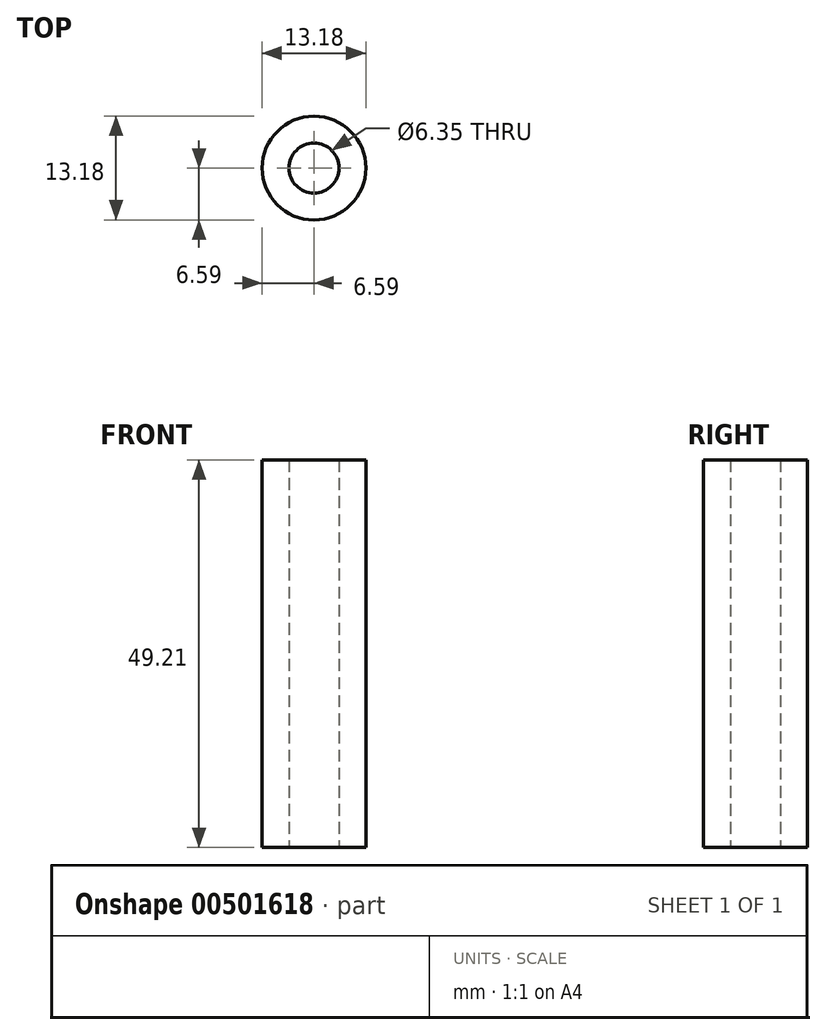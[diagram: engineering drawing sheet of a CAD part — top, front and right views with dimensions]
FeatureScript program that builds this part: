
annotation { "Feature Type Name" : "Feature", "Feature Type Description" : "" }
export const myFeature = defineFeature(function(context is Context, id is Id, definition is map)
    precondition{}
    {
        {
            var Q0;
            Q0=qCreatedBy(makeId("Top.planeOp"),FACE);
            var sketch = newSketch(context, id + "F0", { "sketchPlane" : qUnion([Q0])});
            skCircle(sketch, "E0", {"center": v(0, 0) * mm, "radius": 3.18 * mm});
            skCircle(sketch, "E1", {"center": v(0, 0) * mm, "radius": 6.59 * mm});
            skSolve(sketch);
        }
        {
            var Q0;
            Q0=qSketchRegion(id+"F0",true);
            extrude(context, id + "F1", {"entities" : qUnion([Q0]), "depth" : 49.2 * mm});
        }
    });
